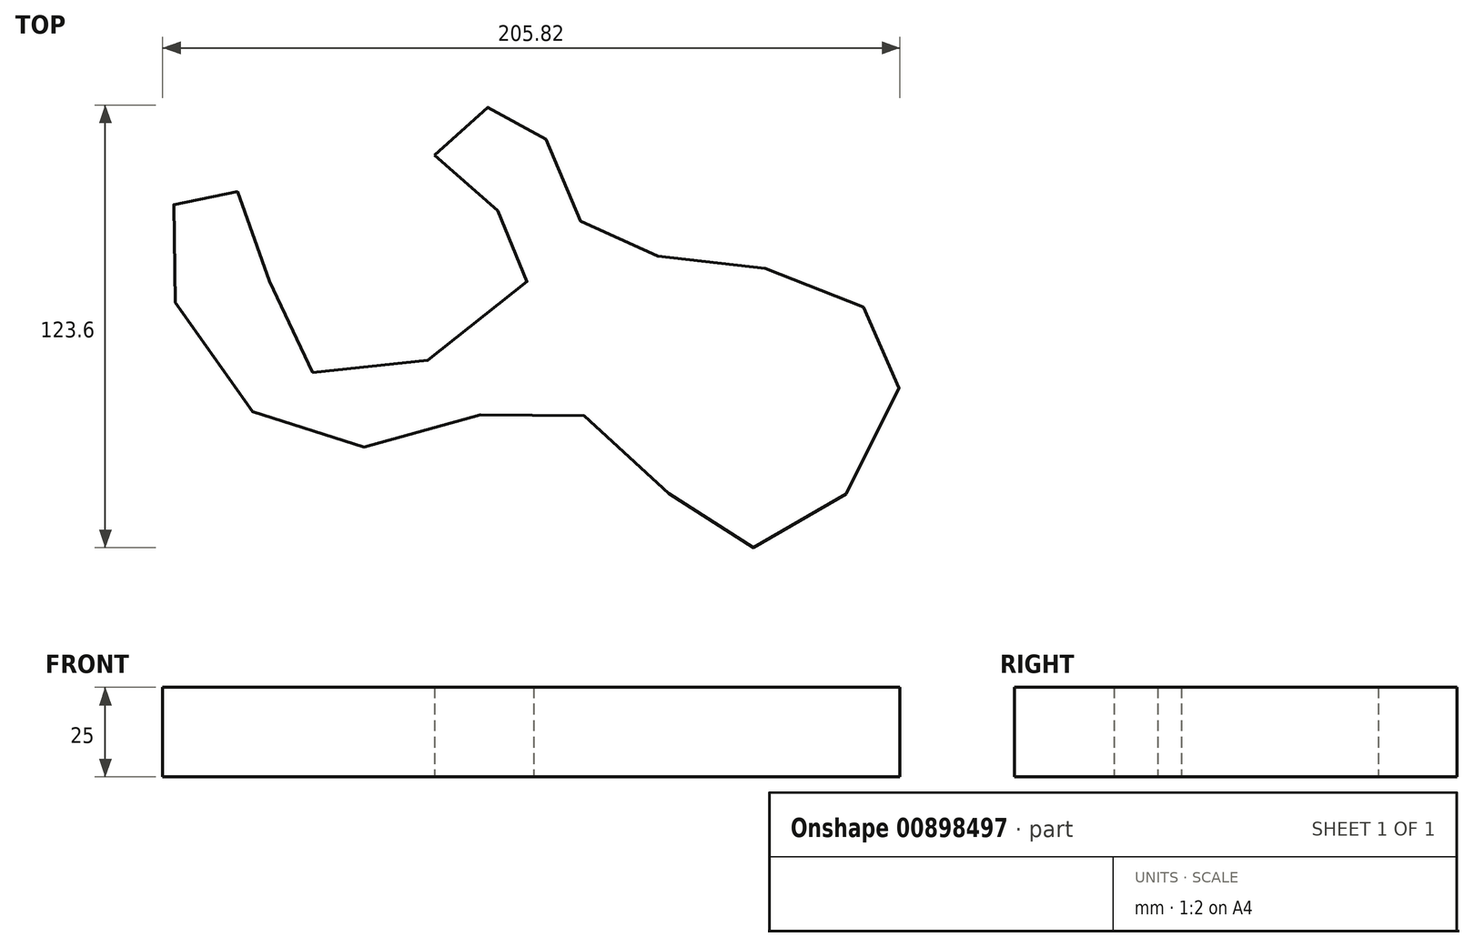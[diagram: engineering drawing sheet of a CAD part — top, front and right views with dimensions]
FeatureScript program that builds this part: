
annotation { "Feature Type Name" : "Feature", "Feature Type Description" : "" }
export const myFeature = defineFeature(function(context is Context, id is Id, definition is map)
    precondition{}
    {
        {
            var Q0;
            Q0=qCreatedBy(makeId("Top.planeOp"),FACE);
            var sketch = newSketch(context, id + "F0", { "sketchPlane" : qUnion([Q0])});
            skFitSpline(sketch, "E0", {"points": [v(-60.11, 43.18) * mm, v(-36.81, 56.54) * mm, v(-18.8, 23.92) * mm, v(32.15, 11.5) * mm, v(69.74, -18.02) * mm, v(28.42, -66.48) * mm, v(-23.14, -27.65) * mm, v(-95.53, -37.28) * mm, v(-134.98, 25.47) * mm, v(-114.16, 32) * mm, v(-92.73, -18.33) * mm, v(-32.46, 14.6) * mm, v(-60.11, 43.18) * mm]});
            skSolve(sketch);
        }
        {
            var Q0;
            Q0=makeQuery(id+"F0.imprint","IMPRINT",FACE,{"disambiguationData":[TD([[makeQuery(id+"F0.imprint","IMPRINT",EDGE,{"derivedFrom":sQuery(id+"F0.wireOp",EDGE,"E0")}),-1.0]])]});
            extrude(context, id + "F1", {"entities" : qUnion([Q0]), "depth" : 25 * mm, "offsetDistance" : 25 * mm});
        }
    });
